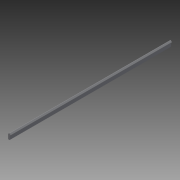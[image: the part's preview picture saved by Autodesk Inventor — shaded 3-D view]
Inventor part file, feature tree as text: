
AUTODESK INVENTOR PART (.ipt)
format: ipt  version: 2016 SP1 (Build 200210100, 210)  size: 99,328 bytes
history: native  units: in
note: dims shown in document units (in); Inventor stores cm internally (conversion verified against a paired STEP export)
features: fillet x1, other x1, imported_body x1
ambient origin geometry x8: Origin, YZ Plane, XZ Plane, XY Plane, X Axis, Y Axis, Z Axis, Center Point
bodies: Body1 (feature_tree)
feature tree (3):
  fillet  "Fillet1"  [1 undecoded]
  other  "BWC-T1-11"
  imported_body  "Base1"
note: 1 required parameter value undecoded (feature->parameter linkage not recoverable at this tier; creation-order binding heuristic only, values carry confidence <= 0.55)
